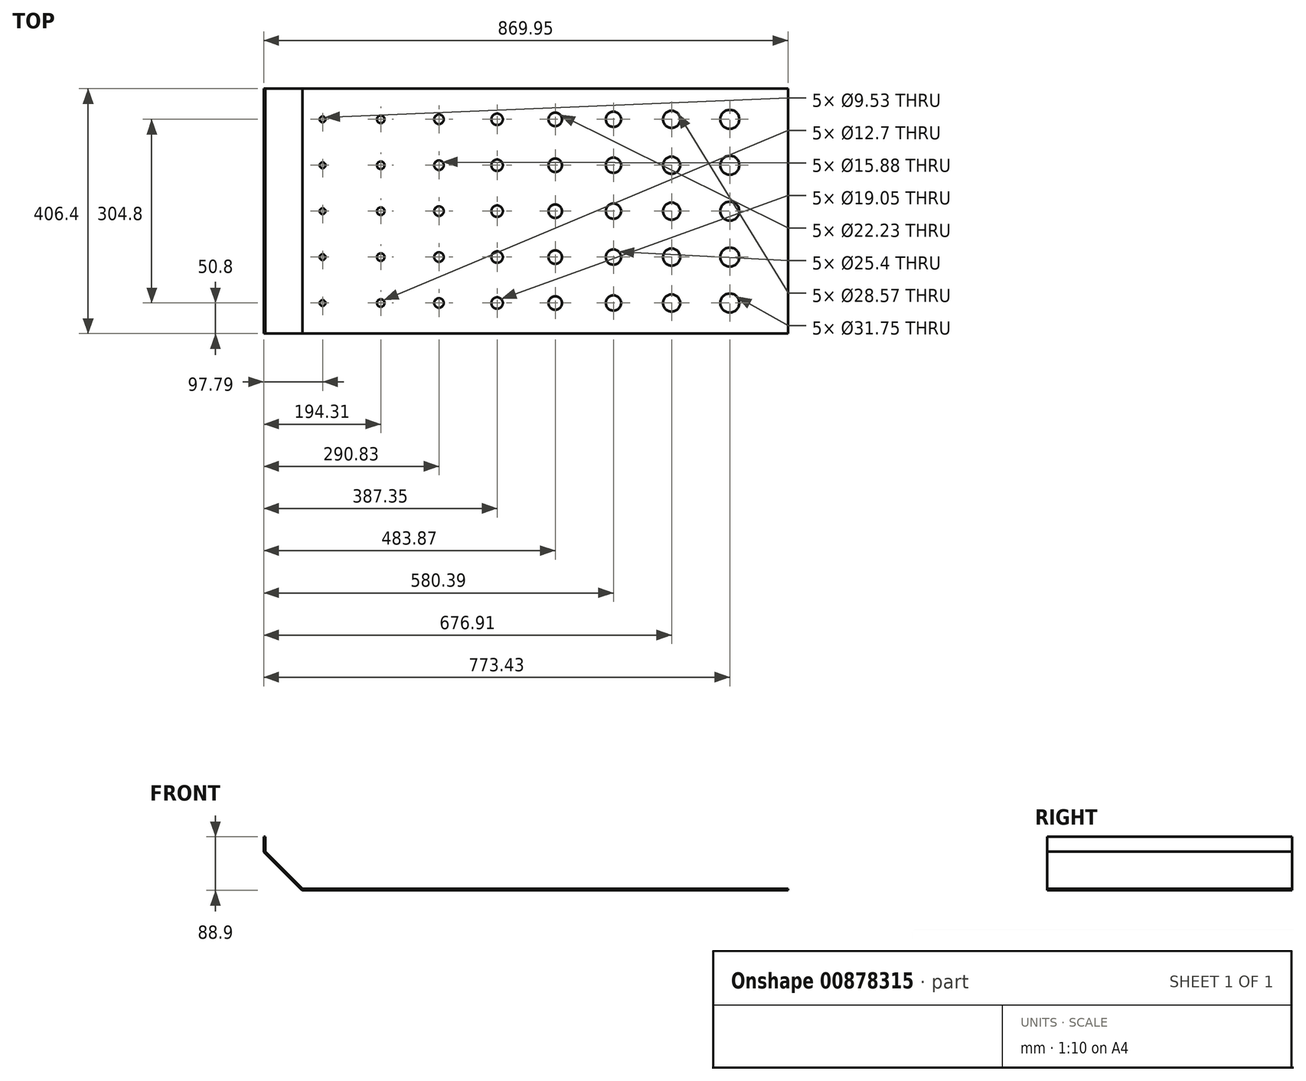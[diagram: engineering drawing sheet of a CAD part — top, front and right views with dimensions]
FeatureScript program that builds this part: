
annotation { "Feature Type Name" : "Feature", "Feature Type Description" : "" }
export const myFeature = defineFeature(function(context is Context, id is Id, definition is map)
    precondition{}
    {
        {
            var Q0;
            Q0=qCreatedBy(makeId("Top.planeOp"),FACE);
            var sketch = newSketch(context, id + "F0", { "sketchPlane" : qUnion([Q0])});
            skLineSegment(sketch, "E0", {"start": v(0, 0) * mm, "end": v(0, -406.4) * mm});
            skLineSegment(sketch, "E1.0", {"start": v(869.95, 0) * mm, "end": v(869.95, -406.4) * mm});
            skLineSegment(sketch, "E2", {"start": v(0, 0) * mm, "end": v(869.95, 0) * mm});
            skLineSegment(sketch, "E3", {"start": v(0, -406.4) * mm, "end": v(869.95, -406.4) * mm});
            skSolve(sketch);
        }
        {
            var Q0;
            Q0=makeQuery(id+"F0.imprint","IMPRINT",FACE,{"disambiguationData":[TD([[makeQuery(id+"F0.imprint","IMPRINT",EDGE,{"derivedFrom":sQuery(id+"F0.wireOp",EDGE,"E0")}),1.0]])]});
            extrude(context, id + "F1", {"entities" : qUnion([Q0]), "depth" : 88.9 * mm, "offsetDistance" : 25.4 * mm});
        }
        {
            var Q0;
            Q0=makeQuery(id+"F1.opExtrude","CAP_EDGE",EDGE,{"disambiguationData":[OSD([sQuery(id+"F0.wireOp",EDGE,"E0")])],"isStart":true});
            chamfer(context, id + "F2", {"entities" : qUnion([Q0]), "width" : 63.5 * mm});
        }
        {
            var Q0;
            Q0=makeQuery(id+"F1.opExtrude","CAP_FACE",FACE,{"disambiguationData":[OSD([sQuery(id+"F0.wireOp",EDGE,"E0"),sQuery(id+"F0.wireOp",EDGE,"E1.0"),sQuery(id+"F0.wireOp",EDGE,"E2"),sQuery(id+"F0.wireOp",EDGE,"E3")])],"isStart":false});
            var Q1;
            Q1=makeQuery(id+"F1.opExtrude","SWEPT_FACE",FACE,{"disambiguationData":[OSD([sQuery(id+"F0.wireOp",EDGE,"E3")])]});
            var Q2;
            Q2=makeQuery(id+"F1.opExtrude","SWEPT_FACE",FACE,{"disambiguationData":[OSD([sQuery(id+"F0.wireOp",EDGE,"E2")])]});
            var Q3;
            Q3=makeQuery(id+"F1.opExtrude","SWEPT_FACE",FACE,{"disambiguationData":[OSD([sQuery(id+"F0.wireOp",EDGE,"E1.0")])]});
            shell(context, id + "F3", {"entities" : qUnion([Q0, Q1, Q2, Q3]), "thickness" : 2.64 * mm});
        }
        {
            var Q0;
            Q0=makeQuery(id+"F3.opShell","OFFSET_FACE",FACE,{"disambiguationData":[OSD([sQuery(id+"F0.wireOp",EDGE,"E0"),sQuery(id+"F0.wireOp",EDGE,"E1.0"),sQuery(id+"F0.wireOp",EDGE,"E2"),sQuery(id+"F0.wireOp",EDGE,"E3")])]});
            var sketch = newSketch(context, id + "F4", { "sketchPlane" : qUnion([Q0])});
            skLineSegment(sketch, "E4.0", {"start": v(773.43, 0) * mm, "end": v(773.43, -406.4) * mm});
            skLineSegment(sketch, "E5.0", {"start": v(676.9, 0) * mm, "end": v(676.9, -406.4) * mm});
            skLineSegment(sketch, "E6.0", {"start": v(580.4, 0) * mm, "end": v(580.4, -406.4) * mm});
            skLineSegment(sketch, "E7.0", {"start": v(483.87, 0) * mm, "end": v(483.87, -406.4) * mm});
            skLineSegment(sketch, "E8.0", {"start": v(387.35, 0) * mm, "end": v(387.35, -406.4) * mm});
            skLineSegment(sketch, "E9.0", {"start": v(290.83, 0) * mm, "end": v(290.83, -406.4) * mm});
            skLineSegment(sketch, "E10.0", {"start": v(194.3, 0) * mm, "end": v(194.3, -406.4) * mm});
            skLineSegment(sketch, "E11.0", {"start": v(97.79, 0) * mm, "end": v(97.79, -406.4) * mm});
            skLineSegment(sketch, "E12.0", {"start": v(64.6, -355.6) * mm, "end": v(869.95, -355.6) * mm});
            skLineSegment(sketch, "E13.0", {"start": v(64.6, -50.8) * mm, "end": v(869.95, -50.8) * mm});
            skLineSegment(sketch, "E14.0", {"start": v(64.6, -279.4) * mm, "end": v(869.95, -279.4) * mm});
            skLineSegment(sketch, "E15.0", {"start": v(64.6, -203.2) * mm, "end": v(869.95, -203.2) * mm});
            skLineSegment(sketch, "E16.0", {"start": v(64.6, -127) * mm, "end": v(869.95, -127) * mm});
            skCircle(sketch, "E17", {"center": v(97.79, -355.6) * mm, "radius": 4.76 * mm});
            skCircle(sketch, "E18", {"center": v(97.79, -279.4) * mm, "radius": 4.76 * mm});
            skCircle(sketch, "E19", {"center": v(97.79, -203.2) * mm, "radius": 4.76 * mm});
            skCircle(sketch, "E20", {"center": v(97.79, -127) * mm, "radius": 4.76 * mm});
            skCircle(sketch, "E21", {"center": v(97.79, -50.8) * mm, "radius": 4.76 * mm});
            skCircle(sketch, "E22", {"center": v(773.43, -50.8) * mm, "radius": 15.88 * mm});
            skCircle(sketch, "E23", {"center": v(773.43, -127) * mm, "radius": 15.88 * mm});
            skCircle(sketch, "E24", {"center": v(773.43, -203.2) * mm, "radius": 15.88 * mm});
            skCircle(sketch, "E25", {"center": v(773.43, -279.4) * mm, "radius": 15.88 * mm});
            skCircle(sketch, "E26", {"center": v(773.43, -355.6) * mm, "radius": 15.88 * mm});
            skCircle(sketch, "E27", {"center": v(194.3, -355.6) * mm, "radius": 6.35 * mm});
            skCircle(sketch, "E28", {"center": v(194.3, -279.4) * mm, "radius": 6.35 * mm});
            skCircle(sketch, "E29", {"center": v(194.3, -203.2) * mm, "radius": 6.35 * mm});
            skCircle(sketch, "E30", {"center": v(194.3, -127) * mm, "radius": 6.35 * mm});
            skCircle(sketch, "E31", {"center": v(194.3, -50.8) * mm, "radius": 6.35 * mm});
            skCircle(sketch, "E32", {"center": v(290.83, -355.6) * mm, "radius": 7.94 * mm});
            skCircle(sketch, "E33", {"center": v(290.83, -279.4) * mm, "radius": 7.94 * mm});
            skCircle(sketch, "E34", {"center": v(290.83, -203.2) * mm, "radius": 7.94 * mm});
            skCircle(sketch, "E35", {"center": v(290.83, -127) * mm, "radius": 7.94 * mm});
            skCircle(sketch, "E36", {"center": v(290.83, -50.8) * mm, "radius": 7.94 * mm});
            skCircle(sketch, "E37", {"center": v(387.35, -50.8) * mm, "radius": 9.53 * mm});
            skCircle(sketch, "E38", {"center": v(387.35, -127) * mm, "radius": 9.53 * mm});
            skCircle(sketch, "E39", {"center": v(387.35, -203.2) * mm, "radius": 9.53 * mm});
            skCircle(sketch, "E40", {"center": v(387.35, -279.4) * mm, "radius": 9.53 * mm});
            skCircle(sketch, "E41", {"center": v(387.35, -355.6) * mm, "radius": 9.53 * mm});
            skCircle(sketch, "E42", {"center": v(483.87, -355.6) * mm, "radius": 11.11 * mm});
            skCircle(sketch, "E43", {"center": v(483.87, -279.4) * mm, "radius": 11.11 * mm});
            skCircle(sketch, "E44", {"center": v(483.87, -203.2) * mm, "radius": 11.11 * mm});
            skCircle(sketch, "E45", {"center": v(483.87, -127) * mm, "radius": 11.11 * mm});
            skCircle(sketch, "E46", {"center": v(483.87, -50.8) * mm, "radius": 11.11 * mm});
            skCircle(sketch, "E47", {"center": v(580.4, -355.6) * mm, "radius": 12.7 * mm});
            skCircle(sketch, "E48", {"center": v(580.4, -279.4) * mm, "radius": 12.7 * mm});
            skCircle(sketch, "E49", {"center": v(580.4, -203.2) * mm, "radius": 12.7 * mm});
            skCircle(sketch, "E50", {"center": v(580.4, -127) * mm, "radius": 12.7 * mm});
            skCircle(sketch, "E51", {"center": v(580.4, -50.8) * mm, "radius": 12.7 * mm});
            skCircle(sketch, "E52", {"center": v(676.9, -50.8) * mm, "radius": 14.29 * mm});
            skCircle(sketch, "E53", {"center": v(676.9, -127) * mm, "radius": 14.29 * mm});
            skCircle(sketch, "E54", {"center": v(676.9, -203.2) * mm, "radius": 14.29 * mm});
            skCircle(sketch, "E55", {"center": v(676.9, -279.4) * mm, "radius": 14.29 * mm});
            skCircle(sketch, "E56", {"center": v(676.9, -355.6) * mm, "radius": 14.29 * mm});
            skSolve(sketch);
        }
        {
            var Q0;
            Q0=sQuery(id+"F4.wireOp",VERTEX,"E21.center");
            var Q1;
            Q1=sQuery(id+"F4.wireOp",VERTEX,"E20.center");
            var Q2;
            Q2=sQuery(id+"F4.wireOp",VERTEX,"E19.center");
            var Q3;
            Q3=sQuery(id+"F4.wireOp",VERTEX,"E18.center");
            var Q4;
            Q4=sQuery(id+"F4.wireOp",VERTEX,"E17.center");
            var Q5;
            Q5=makeQuery(id+"F1.opExtrude","SWEPT_BODY",BODY,{"disambiguationData":[OSD([sQuery(id+"F0.wireOp",EDGE,"E0"),sQuery(id+"F0.wireOp",EDGE,"E1.0"),sQuery(id+"F0.wireOp",EDGE,"E2"),sQuery(id+"F0.wireOp",EDGE,"E3")])]});
            hole(context, id + "F5", {"style" : HoleStyle.SIMPLE, "endStyle" : HoleEndStyle.THROUGH, "holeDiameter" : 9.52 * mm, "majorDiameter" : 6.35 * mm, "isTappedThrough" : true, "tappedDepth" : 12.7 * mm, "tapClearance" : 3, "locations" : qUnion([Q0, Q1, Q2, Q3, Q4]), "scope" : qUnion([Q5])});
        }
        {
            var Q0;
            Q0=sQuery(id+"F4.wireOp",VERTEX,"E31.center");
            var Q1;
            Q1=sQuery(id+"F4.wireOp",VERTEX,"E30.center");
            var Q2;
            Q2=sQuery(id+"F4.wireOp",VERTEX,"E29.center");
            var Q3;
            Q3=sQuery(id+"F4.wireOp",VERTEX,"E28.center");
            var Q4;
            Q4=sQuery(id+"F4.wireOp",VERTEX,"E27.center");
            var Q5;
            Q5=makeQuery(id+"F1.opExtrude","SWEPT_BODY",BODY,{"disambiguationData":[OSD([sQuery(id+"F0.wireOp",EDGE,"E0"),sQuery(id+"F0.wireOp",EDGE,"E1.0"),sQuery(id+"F0.wireOp",EDGE,"E2"),sQuery(id+"F0.wireOp",EDGE,"E3")])]});
            hole(context, id + "F6", {"style" : HoleStyle.SIMPLE, "endStyle" : HoleEndStyle.THROUGH, "holeDiameter" : 12.7 * mm, "majorDiameter" : 6.35 * mm, "isTappedThrough" : true, "tappedDepth" : 12.7 * mm, "tapClearance" : 3, "locations" : qUnion([Q0, Q1, Q2, Q3, Q4]), "scope" : qUnion([Q5])});
        }
        {
            var Q0;
            Q0=sQuery(id+"F4.wireOp",VERTEX,"E36.center");
            var Q1;
            Q1=sQuery(id+"F4.wireOp",VERTEX,"E35.center");
            var Q2;
            Q2=sQuery(id+"F4.wireOp",VERTEX,"E34.center");
            var Q3;
            Q3=sQuery(id+"F4.wireOp",VERTEX,"E33.center");
            var Q4;
            Q4=sQuery(id+"F4.wireOp",VERTEX,"E32.center");
            var Q5;
            Q5=makeQuery(id+"F1.opExtrude","SWEPT_BODY",BODY,{"disambiguationData":[OSD([sQuery(id+"F0.wireOp",EDGE,"E0"),sQuery(id+"F0.wireOp",EDGE,"E1.0"),sQuery(id+"F0.wireOp",EDGE,"E2"),sQuery(id+"F0.wireOp",EDGE,"E3")])]});
            hole(context, id + "F7", {"style" : HoleStyle.SIMPLE, "endStyle" : HoleEndStyle.THROUGH, "holeDiameter" : 15.88 * mm, "majorDiameter" : 6.35 * mm, "isTappedThrough" : true, "tappedDepth" : 12.7 * mm, "tapClearance" : 3, "locations" : qUnion([Q0, Q1, Q2, Q3, Q4]), "scope" : qUnion([Q5])});
        }
        {
            var Q0;
            Q0=sQuery(id+"F4.wireOp",VERTEX,"E41.center");
            var Q1;
            Q1=sQuery(id+"F4.wireOp",VERTEX,"E40.center");
            var Q2;
            Q2=sQuery(id+"F4.wireOp",VERTEX,"E39.center");
            var Q3;
            Q3=sQuery(id+"F4.wireOp",VERTEX,"E38.center");
            var Q4;
            Q4=sQuery(id+"F4.wireOp",VERTEX,"E37.center");
            var Q5;
            Q5=makeQuery(id+"F1.opExtrude","SWEPT_BODY",BODY,{"disambiguationData":[OSD([sQuery(id+"F0.wireOp",EDGE,"E0"),sQuery(id+"F0.wireOp",EDGE,"E1.0"),sQuery(id+"F0.wireOp",EDGE,"E2"),sQuery(id+"F0.wireOp",EDGE,"E3")])]});
            hole(context, id + "F8", {"style" : HoleStyle.SIMPLE, "endStyle" : HoleEndStyle.THROUGH, "holeDiameter" : 19.05 * mm, "majorDiameter" : 6.35 * mm, "isTappedThrough" : true, "tappedDepth" : 12.7 * mm, "tapClearance" : 3, "locations" : qUnion([Q0, Q1, Q2, Q3, Q4]), "scope" : qUnion([Q5])});
        }
        {
            var Q0;
            Q0=sQuery(id+"F4.wireOp",VERTEX,"E42.center");
            var Q1;
            Q1=sQuery(id+"F4.wireOp",VERTEX,"E43.center");
            var Q2;
            Q2=sQuery(id+"F4.wireOp",VERTEX,"E44.center");
            var Q3;
            Q3=sQuery(id+"F4.wireOp",VERTEX,"E45.center");
            var Q4;
            Q4=sQuery(id+"F4.wireOp",VERTEX,"E46.center");
            var Q5;
            Q5=makeQuery(id+"F1.opExtrude","SWEPT_BODY",BODY,{"disambiguationData":[OSD([sQuery(id+"F0.wireOp",EDGE,"E0"),sQuery(id+"F0.wireOp",EDGE,"E1.0"),sQuery(id+"F0.wireOp",EDGE,"E2"),sQuery(id+"F0.wireOp",EDGE,"E3")])]});
            hole(context, id + "F9", {"style" : HoleStyle.SIMPLE, "endStyle" : HoleEndStyle.THROUGH, "holeDiameter" : 22.22 * mm, "majorDiameter" : 6.35 * mm, "isTappedThrough" : true, "tappedDepth" : 12.7 * mm, "tapClearance" : 3, "locations" : qUnion([Q0, Q1, Q2, Q3, Q4]), "scope" : qUnion([Q5])});
        }
        {
            var Q0;
            Q0=sQuery(id+"F4.wireOp",VERTEX,"E47.center");
            var Q1;
            Q1=sQuery(id+"F4.wireOp",VERTEX,"E48.center");
            var Q2;
            Q2=sQuery(id+"F4.wireOp",VERTEX,"E49.center");
            var Q3;
            Q3=sQuery(id+"F4.wireOp",VERTEX,"E50.center");
            var Q4;
            Q4=sQuery(id+"F4.wireOp",VERTEX,"E51.center");
            var Q5;
            Q5=makeQuery(id+"F1.opExtrude","SWEPT_BODY",BODY,{"disambiguationData":[OSD([sQuery(id+"F0.wireOp",EDGE,"E0"),sQuery(id+"F0.wireOp",EDGE,"E1.0"),sQuery(id+"F0.wireOp",EDGE,"E2"),sQuery(id+"F0.wireOp",EDGE,"E3")])]});
            hole(context, id + "F10", {"style" : HoleStyle.SIMPLE, "endStyle" : HoleEndStyle.THROUGH, "holeDiameter" : 25.4 * mm, "majorDiameter" : 6.35 * mm, "isTappedThrough" : true, "tappedDepth" : 12.7 * mm, "tapClearance" : 3, "locations" : qUnion([Q0, Q1, Q2, Q3, Q4]), "scope" : qUnion([Q5])});
        }
        {
            var Q0;
            Q0=sQuery(id+"F4.wireOp",VERTEX,"E56.center");
            var Q1;
            Q1=sQuery(id+"F4.wireOp",VERTEX,"E55.center");
            var Q2;
            Q2=sQuery(id+"F4.wireOp",VERTEX,"E54.center");
            var Q3;
            Q3=sQuery(id+"F4.wireOp",VERTEX,"E53.center");
            var Q4;
            Q4=sQuery(id+"F4.wireOp",VERTEX,"E52.center");
            var Q5;
            Q5=makeQuery(id+"F1.opExtrude","SWEPT_BODY",BODY,{"disambiguationData":[OSD([sQuery(id+"F0.wireOp",EDGE,"E0"),sQuery(id+"F0.wireOp",EDGE,"E1.0"),sQuery(id+"F0.wireOp",EDGE,"E2"),sQuery(id+"F0.wireOp",EDGE,"E3")])]});
            hole(context, id + "F11", {"style" : HoleStyle.SIMPLE, "endStyle" : HoleEndStyle.THROUGH, "holeDiameter" : 28.57 * mm, "majorDiameter" : 6.35 * mm, "isTappedThrough" : true, "tappedDepth" : 12.7 * mm, "tapClearance" : 3, "locations" : qUnion([Q0, Q1, Q2, Q3, Q4]), "scope" : qUnion([Q5])});
        }
        {
            var Q0;
            Q0=sQuery(id+"F4.wireOp",VERTEX,"E26.center");
            var Q1;
            Q1=sQuery(id+"F4.wireOp",VERTEX,"E25.center");
            var Q2;
            Q2=sQuery(id+"F4.wireOp",VERTEX,"E24.center");
            var Q3;
            Q3=sQuery(id+"F4.wireOp",VERTEX,"E23.center");
            var Q4;
            Q4=sQuery(id+"F4.wireOp",VERTEX,"E22.center");
            var Q5;
            Q5=makeQuery(id+"F1.opExtrude","SWEPT_BODY",BODY,{"disambiguationData":[OSD([sQuery(id+"F0.wireOp",EDGE,"E0"),sQuery(id+"F0.wireOp",EDGE,"E1.0"),sQuery(id+"F0.wireOp",EDGE,"E2"),sQuery(id+"F0.wireOp",EDGE,"E3")])]});
            hole(context, id + "F12", {"style" : HoleStyle.SIMPLE, "endStyle" : HoleEndStyle.THROUGH, "holeDiameter" : 31.75 * mm, "majorDiameter" : 6.35 * mm, "isTappedThrough" : true, "tappedDepth" : 12.7 * mm, "tapClearance" : 3, "locations" : qUnion([Q0, Q1, Q2, Q3, Q4]), "scope" : qUnion([Q5])});
        }
    });
